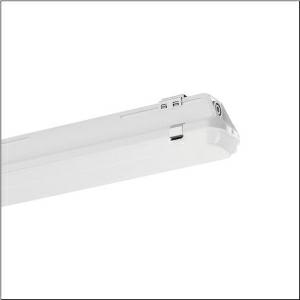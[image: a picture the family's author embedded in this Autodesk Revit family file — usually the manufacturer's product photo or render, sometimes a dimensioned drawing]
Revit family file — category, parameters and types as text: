
# Revit family: monsun_r__21_parking_51fg20dp440bhr_9634
name_source: partatom
category: Lighting Fixtures
units: mm (PartAtom-declared; Revit-internal decimal feet)

## family parameters
Cut with Voids When Loaded = No
Host = Face
Light Source = No
Part Type = Normal
Room Calculation Point = No
Round Connector Dimension = Use Diameter
Shared = No

## types (1)
- --- (1 x LED, 4810 lm, 34.9 W, 4000K)
    Apparent Load = 35 VA
    CIE Flux Codes = 45 75 93 94 100
    Color Rendering = 80
    Color Temperature = 4000K
    Default Elevation = 1800 mm
    Description = Monsun® 21 parking, damp-proof luminaire, chain hanger, primary optical cover: enclosure, of PC, light emission: direct distribution, primary light characteristic: symmetric, installation type: vertical mounting, horizontal mounting, surface-mounted, suspended mounting, LED, rated luminous flux: 4.810lm, luminous efficacy: 140lm/W, light colour: 840, colour temperature: 4000K, control gear: ECG DALI, with terminal, 5-pole, max. 2.5mm², mains connection: 220..240V, AC, 50/60Hz, rated input power: 34W, housing, of glass-fibre reinforced polyester, uncoated, bright grey, length: 1.590mm, width: 90mm, height: 88mm, clip for enclosure, of stainless steel (V2A), ceiling mounting element, of stainless steel (V2A), chain hanger, of stainless steel (V2A), multi-sensor HC1, local control, protection rating (complete): IP66, insulation class (complete): insulation class I (protective earthing), certification: CE, ENEC, VDE, UKCA, protection symbol: D, impact resistance: IK08, permissible operating ambient temperature: -25..+35°C, standard: EN 50419, EN 60598-2-1, no direct snow, no direct sun, no direct rain, for indoor or canopied outdoor use, corresponds to IFS (International Featured Standards) requirements for safety and quality in the food industry, packaging unit: 1 piece
    Height = 89 mm
    Lamp = 1 x LED
    Lamp Light Flux = 4810 lm
    Lamp Power = 34.9 W
    Lamp count = 1
    Length = 1590 mm
    Luminous efficacy = 138 lm/W
    Manufacturer = Siteco
    ModVariant = No
    Model = 51FG20DP440BHR
    Mounting Place = Ceiling
    Mounting Type = Pendant
    Number of Poles = 1
    OnlyDefault = Yes
    Power Factor = 1
    Product Name = Monsun® 21 parking
    Product group = damp-proof luminaire | ceiling pendant
    ProductGroupID = 908
    Protection Class = Protection class I
    Protection Degree = IP 66
    RLX_Detail_Level = 1
    RlxData = <blob elided: 92145 chars, md5=7bbc4c91>
    Socket = socket
    Standby Power = 0 W
    System Light Flux = 4810 lm
    System Power = 35 W
    Type Comments = factory setting: luminous flux: 100 % | dim-lin: 254 | 228 mA
    Type Image = l_1006717.jpg
    URL = http://relux.com
    VarID = @adj_049729
    Voltage = 0 V
    Weight = 0.00 kg
    Width = 90 mm

## geometry (parser evidence)
native form markers: Blend x4, Sweep x16
no freeform markers — native parametric forms only
